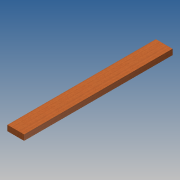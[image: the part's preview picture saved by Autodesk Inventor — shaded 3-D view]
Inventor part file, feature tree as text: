
AUTODESK INVENTOR PART (.ipt)
format: ipt  version: 2014 SP1 (Build 180222100, 222)  size: 75,264 bytes
history: native  units: in
note: dims shown in document units (in); Inventor stores cm internally (conversion verified against a paired STEP export)
features: extrude x1, sketch x1
ambient origin geometry x8: Origin, YZ Plane, XZ Plane, XY Plane, X Axis, Y Axis, Z Axis, Center Point
bodies: Solid1 (feature_tree)
feature tree (2):
  extrude  "Extrusion1"  Depth=1.4961in
  sketch  "Sketch1"  dims[d0=4.4882in d1=1.4961in d2=40.0in d3=0.0in]
